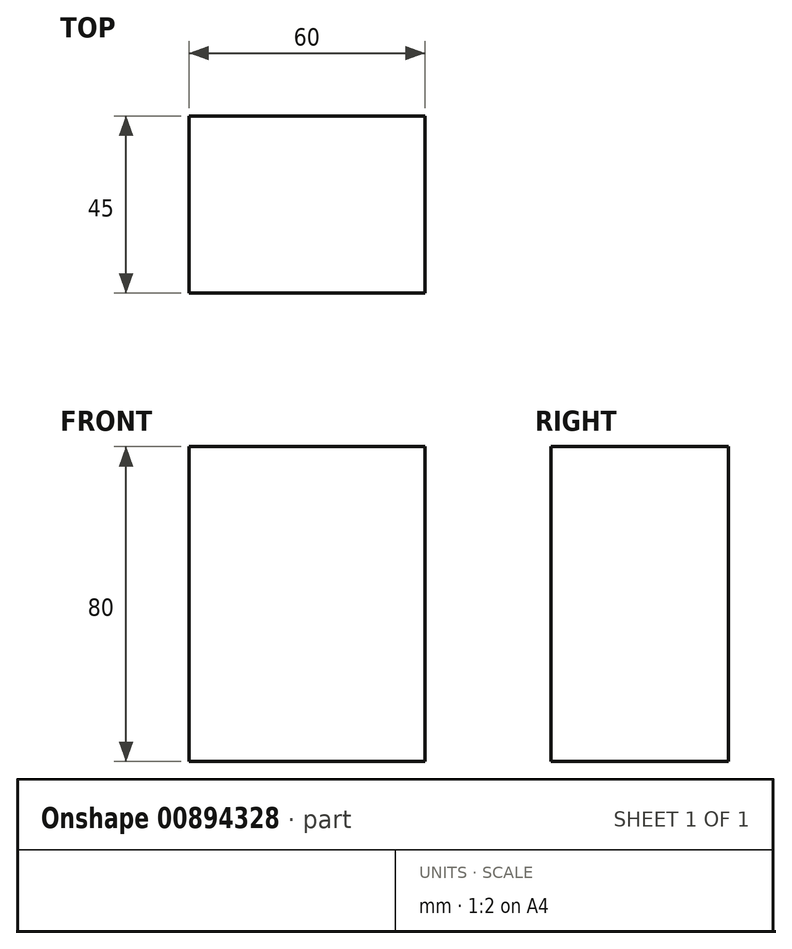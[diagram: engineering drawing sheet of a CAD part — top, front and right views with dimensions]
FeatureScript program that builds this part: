
annotation { "Feature Type Name" : "Feature", "Feature Type Description" : "" }
export const myFeature = defineFeature(function(context is Context, id is Id, definition is map)
    precondition{}
    {
        {
            var Q0;
            Q0=qCreatedBy(makeId("Front.planeOp"),FACE);
            var sketch = newSketch(context, id + "F0", { "sketchPlane" : qUnion([Q0])});
            skLineSegment(sketch, "E0.bottom", {"start": v(0, 0) * mm, "end": v(60, 0) * mm});
            skLineSegment(sketch, "E0.top", {"start": v(0, 80) * mm, "end": v(60, 80) * mm});
            skLineSegment(sketch, "E0.left", {"start": v(0, 0) * mm, "end": v(0, 80) * mm});
            skLineSegment(sketch, "E0.right", {"start": v(60, 0) * mm, "end": v(60, 80) * mm});
            skSolve(sketch);
        }
        {
            var Q0;
            Q0 = qSketchRegion(id + "F0", true);
            extrude(context, id + "F1", {"entities" : qUnion([Q0]), "depth" : 45 * mm, "offsetDistance" : 25 * mm});
        }
    });
